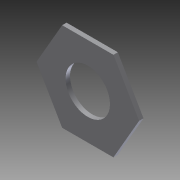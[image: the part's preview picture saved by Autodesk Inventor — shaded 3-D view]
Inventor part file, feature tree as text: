
AUTODESK INVENTOR PART (.ipt)
format: ipt  version: 2012 (Build 160160000, 160)  size: 79,360 bytes
history: native  units: in
note: dims shown in document units (in); Inventor stores cm internally (conversion verified against a paired STEP export)
features: extrude x1, sketch x1
ambient origin geometry x8: Origin, YZ Plane, XZ Plane, XY Plane, X Axis, Y Axis, Z Axis, Center Point
bodies: Solid1 (feature_tree)
feature tree (2):
  extrude  "Extrusion1"  Depth=2.5in
  sketch  "Sketch1"  dims[d3=0.125in d4=0.0in d5=2.5in d6=1.25in]
